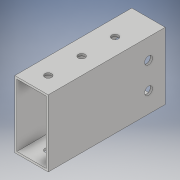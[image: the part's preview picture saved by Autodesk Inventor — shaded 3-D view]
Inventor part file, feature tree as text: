
AUTODESK INVENTOR PART (.ipt)
format: ipt  version: 2018 (Build 220112000, 112)  size: 125,952 bytes
history: native  units: in
note: dims shown in document units (in); Inventor stores cm internally (conversion verified against a paired STEP export)
features: extrude x3, sketch x3
ambient origin geometry x8: Origin, YZ Plane, XZ Plane, XY Plane, X Axis, Y Axis, Z Axis, Center Point
bodies: Solid1 (feature_tree)
feature tree (6):
  extrude  "Extrusion1"  Depth=2.0in
  extrude  "Extrusion2"  Depth=3.5in TaperAngle=0.0deg
  extrude  "Extrusion3"  Depth=0.3937in
  sketch  "Sketch1"  dims[d0=1.0in d1=2.0in]
  sketch  "Sketch2"  dims[d2=0.0625in d3=3.5in d4=0.0in]
  sketch  "Sketch3"  dims[d5=0.5in d6=0.3937in d7=0.7874in d8=0.2362in d9=3.5in d10=0.0in d11=0.5in d12=1.0in d13=1.0in d14=0.2031in d15=3.5in d16=0.0in]
